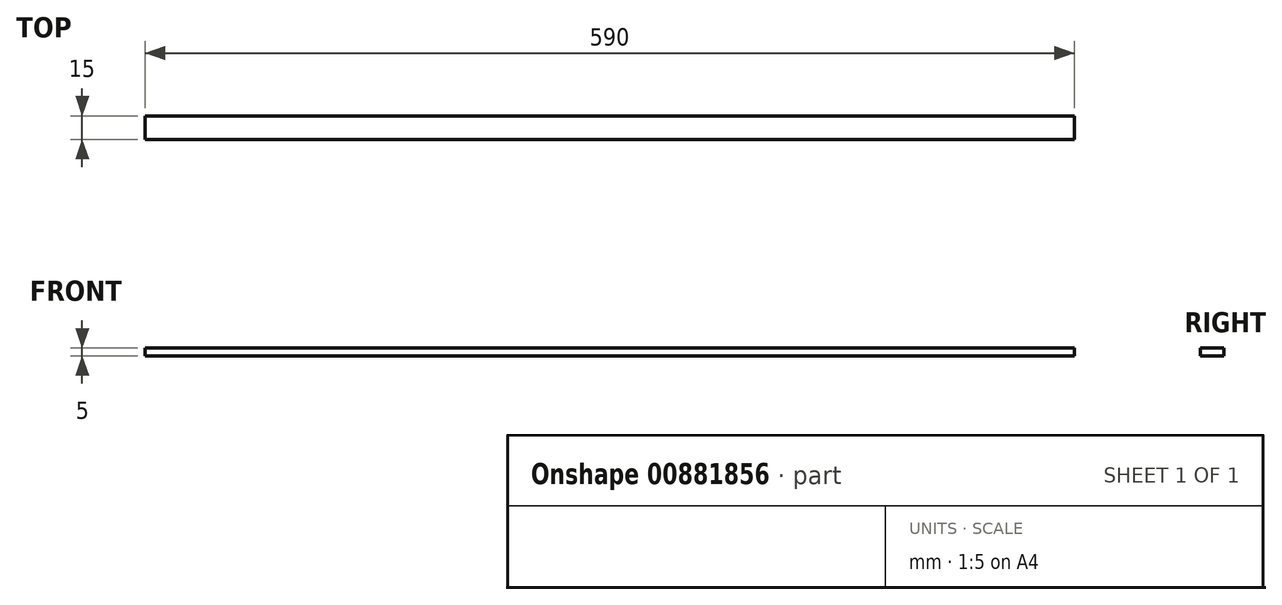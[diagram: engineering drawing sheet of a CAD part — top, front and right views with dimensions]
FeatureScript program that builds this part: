
annotation { "Feature Type Name" : "Feature", "Feature Type Description" : "" }
export const myFeature = defineFeature(function(context is Context, id is Id, definition is map)
    precondition{}
    {
        {
            var Q0;
            Q0=qCreatedBy(makeId("Top.planeOp"),FACE);
            var sketch = newSketch(context, id + "F0", { "sketchPlane" : qUnion([Q0])});
            skLineSegment(sketch, "E0.bottom", {"start": v(-18.5, 4.73) * mm, "end": v(571.5, 4.73) * mm});
            skLineSegment(sketch, "E0.top", {"start": v(-18.5, -10.27) * mm, "end": v(571.5, -10.27) * mm});
            skLineSegment(sketch, "E0.left", {"start": v(-18.5, 4.73) * mm, "end": v(-18.5, -10.27) * mm});
            skLineSegment(sketch, "E0.right", {"start": v(571.5, 4.73) * mm, "end": v(571.5, -10.27) * mm});
            skSolve(sketch);
        }
        {
            var Q0;
            Q0=qSketchRegion(id+"F0",true);
            extrude(context, id + "F1", {"entities" : qUnion([Q0]), "depth" : 5 * mm, "offsetDistance" : 25 * mm});
        }
    });
